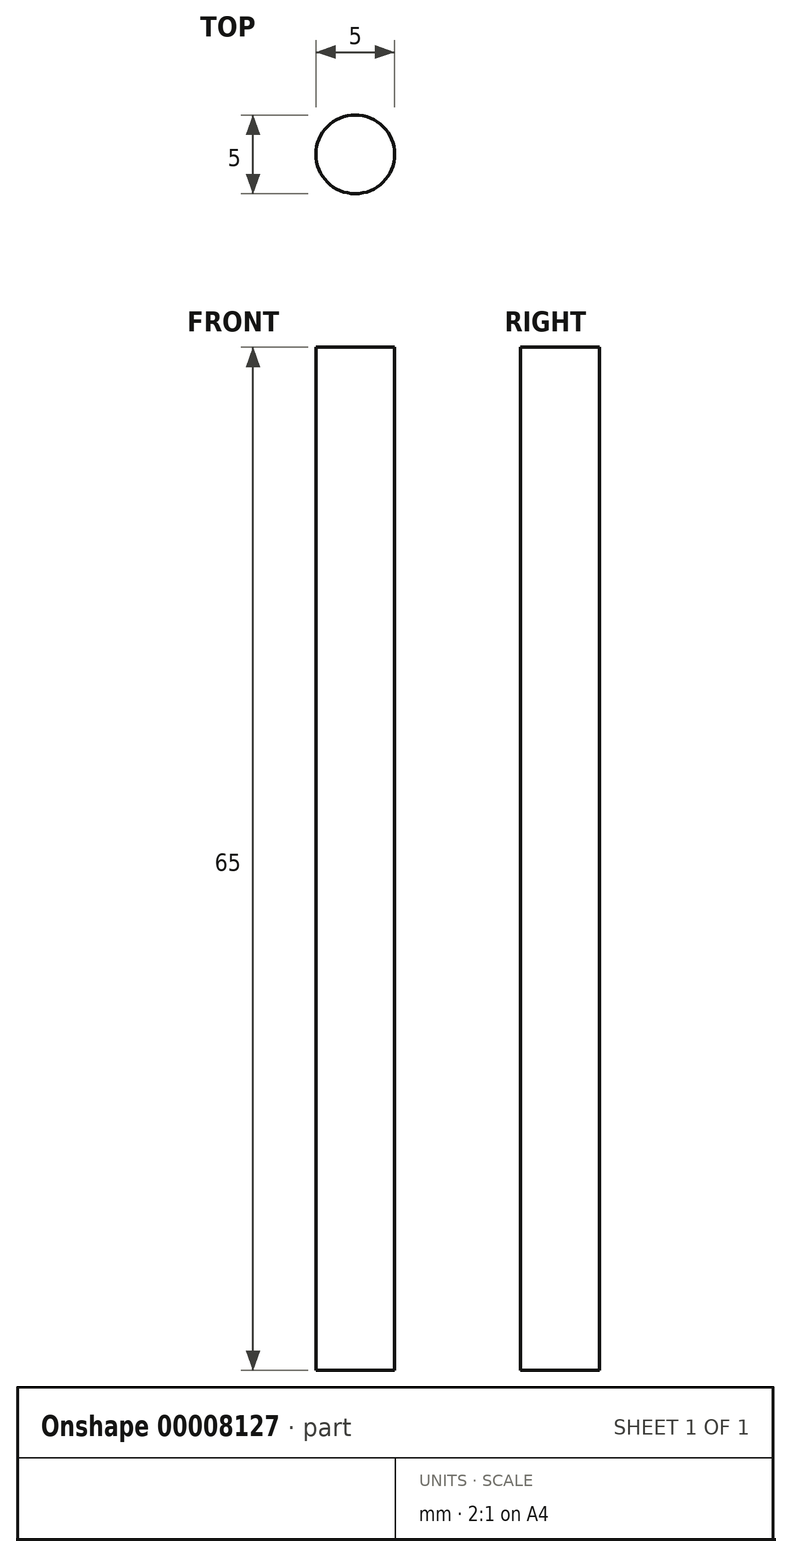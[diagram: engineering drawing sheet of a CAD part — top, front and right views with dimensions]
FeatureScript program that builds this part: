
annotation { "Feature Type Name" : "Feature", "Feature Type Description" : "" }
export const myFeature = defineFeature(function(context is Context, id is Id, definition is map)
    precondition{}
    {
        {
            var Q0;
            Q0=qCreatedBy(makeId("Top.planeOp"),FACE);
            var sketch = newSketch(context, id + "F0", { "sketchPlane" : qUnion([Q0])});
            skCircle(sketch, "E0", {"center": v(0, 0) * mm, "radius": 2.5 * mm});
            skSolve(sketch);
        }
        {
            var Q0;
            Q0 = qSketchRegion(id + "F0", true);
            extrude(context, id + "F1", {"entities" : qUnion([Q0]), "depth" : 65 * mm, "offsetDistance" : 25 * mm});
        }
    });
